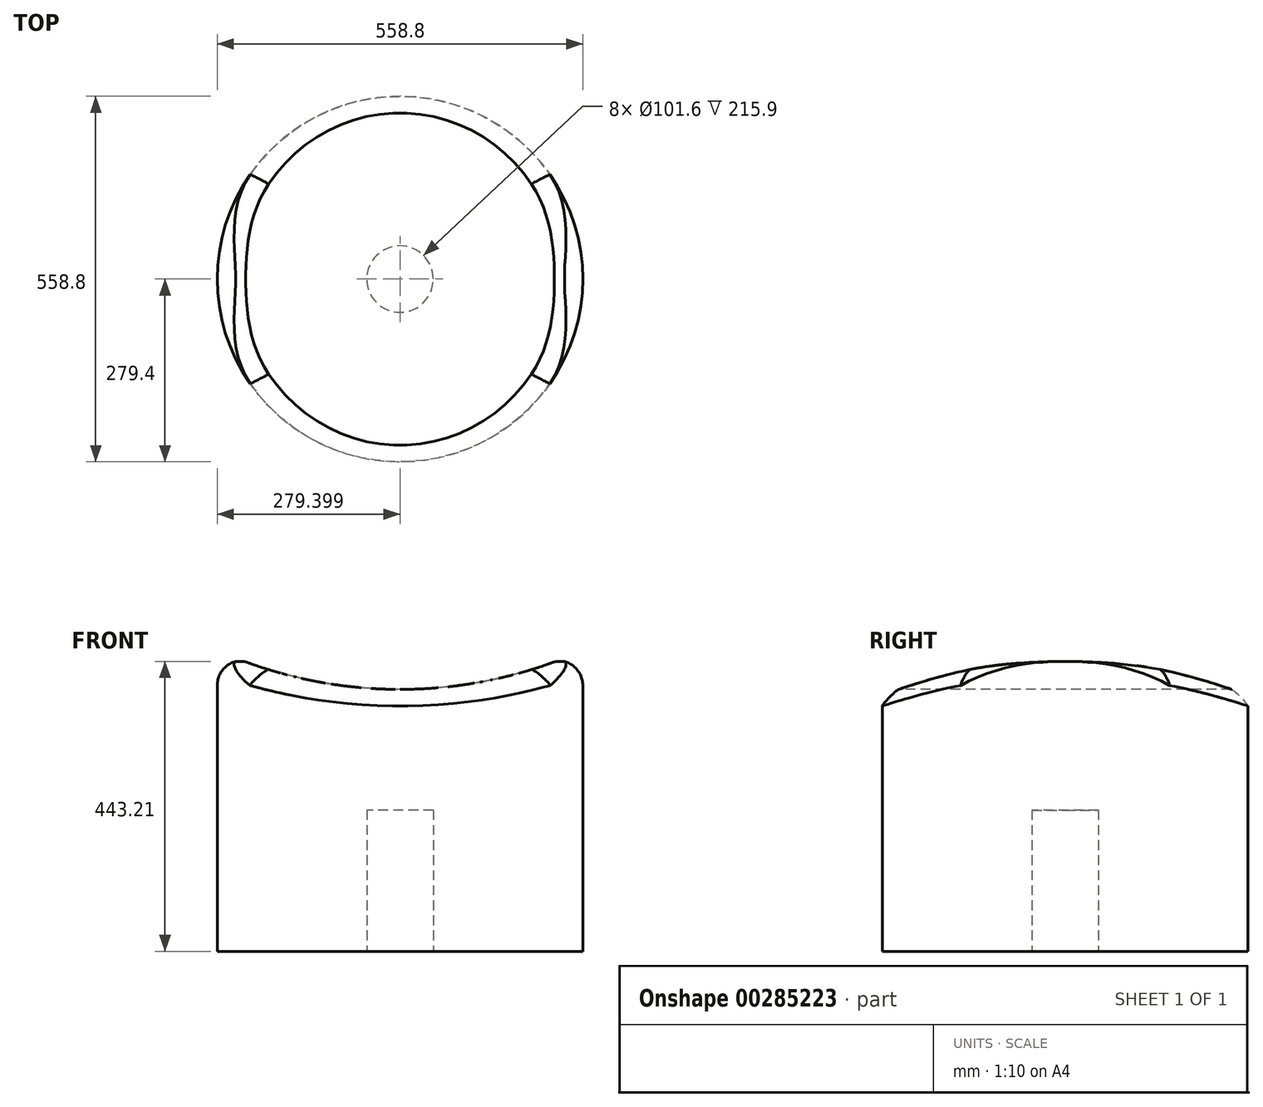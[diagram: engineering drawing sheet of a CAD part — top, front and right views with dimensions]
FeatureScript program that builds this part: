
annotation { "Feature Type Name" : "Feature", "Feature Type Description" : "" }
export const myFeature = defineFeature(function(context is Context, id is Id, definition is map)
    precondition{}
    {
        {
            var Q0;
            Q0=qCreatedBy(makeId("Top.planeOp"),FACE);
            var sketch = newSketch(context, id + "F0", { "sketchPlane" : qUnion([Q0])});
            skCircle(sketch, "E0", {"center": v(11.45, 0) * mm, "radius": 279.4 * mm});
            skSolve(sketch);
        }
        {
            var Q0;
            Q0=makeQuery(id+"F0.imprint","IMPRINT",FACE,{"disambiguationData":[TD([[makeQuery(id+"F0.imprint","IMPRINT",EDGE,{"derivedFrom":sQuery(id+"F0.wireOp",EDGE,"E0")}),1.0]])]});
            extrude(context, id + "F1", {"entities" : qUnion([Q0]), "endBound" : BoundingType.SYMMETRIC, "depth" : 444.5 * mm});
        }
        {
            var Q0;
            Q0=makeQuery(id+"F1.opExtrude","CAP_EDGE",EDGE,{"disambiguationData":[OSD([sQuery(id+"F0.wireOp",EDGE,"E0")])],"isStart":false});
            fillet(context, id + "F2", {"entities" : qUnion([Q0]), "radius" : 38.1 * mm, "tangentPropagation" : true, "allowEdgeOverflow" : false});
        }
        {
            var Q0;
            Q0=makeQuery(id+"F1.opExtrude","CAP_FACE",FACE,{"disambiguationData":[OSD([sQuery(id+"F0.wireOp",EDGE,"E0")])],"isStart":true});
            shell(context, id + "F3", {"entities" : qUnion([Q0]), "thickness" : 228.6 * mm});
        }
        {
            var Q0;
            Q0=qCreatedBy(makeId("Front.planeOp"),FACE);
            var sketch = newSketch(context, id + "F4", { "sketchPlane" : qUnion([Q0])});
            skCircle(sketch, "E1", {"center": v(11.45, 860.28) * mm, "radius": 682.13 * mm});
            skPoint(sketch, "E1.first.point", {"position": v(-229.85, 222.25) * mm});
            skPoint(sketch, "E1.second.point", {"position": v(252.75, 222.25) * mm});
            skPoint(sketch, "E1.third.point", {"position": v(0, 178.24) * mm});
            skSolve(sketch);
        }
        {
            var Q0;
            Q0 = qSketchRegion(id + "F4", true);
            extrude(context, id + "F5", {"entities" : qUnion([Q0]), "operationType" : NewBodyOperationType.REMOVE, "endBound" : BoundingType.SYMMETRIC, "oppositeDirection" : true, "depth" : 584.2 * mm});
        }
        {
            var Q0;
            Q0=makeQuery(id+"F5.boolean.opBoolean","INTERSECT",EDGE,{"disambiguationData":[OD(0.0)],"derivedFrom":[makeQuery(id+"F1.opExtrude","SWEPT_FACE",FACE,{"disambiguationData":[OSD([sQuery(id+"F0.wireOp",EDGE,"E0")])]}),makeQuery(id+"F5.opExtrude","SWEPT_FACE",FACE,{"disambiguationData":[OSD([sQuery(id+"F4.wireOp",EDGE,"E1")])]})]});
            fillet(context, id + "F6", {"entities" : qUnion([Q0]), "radius" : 25.4 * mm, "tangentPropagation" : true, "rho" : .1, "crossSection" : FilletCrossSection.CONIC, "allowEdgeOverflow" : false});
        }
    });
